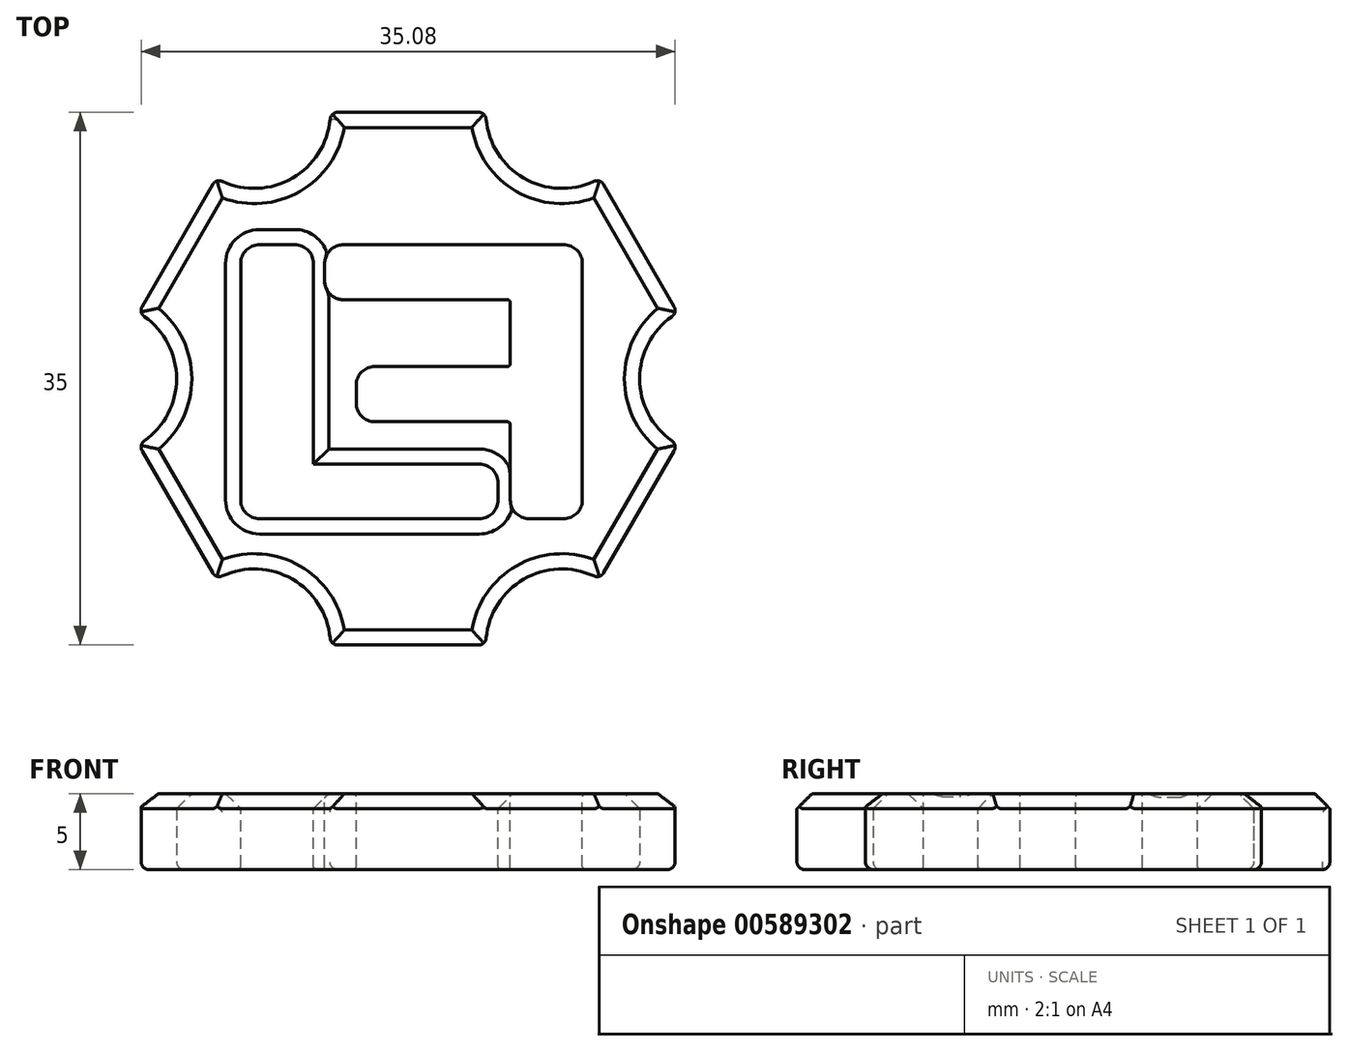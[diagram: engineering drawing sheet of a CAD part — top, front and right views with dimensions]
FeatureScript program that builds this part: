
annotation { "Feature Type Name" : "Feature", "Feature Type Description" : "" }
export const myFeature = defineFeature(function(context is Context, id is Id, definition is map)
    precondition{}
    {
        {
            var Q0;
            Q0=qCreatedBy(makeId("Top.planeOp"),FACE);
            var sketch = newSketch(context, id + "F0", { "sketchPlane" : qUnion([Q0])});
            skCircle(sketch, "E0.cCircle", {"center": v(0, 0) * mm, "radius": 17.5 * mm, "construction": true});
            skLineSegment(sketch, "E0.0", {"start": v(10.1, -17.5) * mm, "end": v(-10.1, -17.5) * mm});
            skLineSegment(sketch, "E0.1", {"start": v(-10.1, -17.5) * mm, "end": v(-20.2, 0) * mm});
            skLineSegment(sketch, "E0.2", {"start": v(-20.2, 0) * mm, "end": v(-10.1, 17.5) * mm});
            skLineSegment(sketch, "E0.3", {"start": v(-10.1, 17.5) * mm, "end": v(10.1, 17.5) * mm});
            skLineSegment(sketch, "E0.4", {"start": v(10.1, 17.5) * mm, "end": v(20.2, 0) * mm});
            skLineSegment(sketch, "E0.5", {"start": v(20.2, 0) * mm, "end": v(10.1, -17.5) * mm});
            skPoint(sketch, "E0.0.midPoint", {"position": v(0, -17.5) * mm});
            skCircle(sketch, "E1", {"center": v(-10.1, 17.5) * mm, "radius": 5 * mm});
            skCircle(sketch, "E2", {"center": v(-20.2, 0) * mm, "radius": 5 * mm});
            skCircle(sketch, "E3", {"center": v(-10.1, -17.5) * mm, "radius": 5 * mm});
            skCircle(sketch, "E4", {"center": v(10.1, -17.5) * mm, "radius": 5 * mm});
            skCircle(sketch, "E5", {"center": v(20.2, 0) * mm, "radius": 5 * mm});
            skCircle(sketch, "E6", {"center": v(10.1, 17.5) * mm, "radius": 5 * mm});
            skSolve(sketch);
        }
        {
            var Q0;
            {var subQ1=sQuery(id+"F0.wireOp",EDGE,"E0.0");var subQ13=sQuery(id+"F0.wireOp",EDGE,"E4");var subQ15=makeQuery(id+"F0.imprint","INTERSECT",VERTEX,{"derivedFrom":[subQ1,subQ13]});Q0=makeQuery(id+"F0.imprint","IMPRINT",FACE,{"disambiguationData":[TD([[makeQuery(id+"F0.imprint","IMPRINT",EDGE,{"disambiguationData":[TD([[subQ15,-1.0]])],"derivedFrom":subQ1}),-1.0]])]});}
            extrude(context, id + "F1", {"entities" : qUnion([Q0]), "endBound" : BoundingType.SYMMETRIC, "depth" : 5 * mm, "offsetDistance" : 25 * mm});
        }
        {
            var Q0;
            Q0=makeQuery(id+"F1.opExtrude","CAP_FACE",FACE,{"disambiguationData":[OSD([sQuery(id+"F0.wireOp",EDGE,"E0.0"),sQuery(id+"F0.wireOp",EDGE,"E0.1"),sQuery(id+"F0.wireOp",EDGE,"E0.2"),sQuery(id+"F0.wireOp",EDGE,"E0.3"),sQuery(id+"F0.wireOp",EDGE,"E0.4"),sQuery(id+"F0.wireOp",EDGE,"E0.5"),sQuery(id+"F0.wireOp",EDGE,"E1"),sQuery(id+"F0.wireOp",EDGE,"E2"),sQuery(id+"F0.wireOp",EDGE,"E3"),sQuery(id+"F0.wireOp",EDGE,"E4"),sQuery(id+"F0.wireOp",EDGE,"E5"),sQuery(id+"F0.wireOp",EDGE,"E6")])],"isStart":false});
            var sketch = newSketch(context, id + "F2", { "sketchPlane" : qUnion([Q0])});
            skLineSegment(sketch, "E7", {"start": v(4.67, -5.61) * mm, "end": v(-6.22, -5.61) * mm});
            skArc(sketch, "E8", {"start": v(5.9, -6.85) * mm, "mid": v(5.54, -5.98) * mm, "end": v(4.67, -5.61) * mm});
            skLineSegment(sketch, "E9", {"start": v(5.9, -7.96) * mm, "end": v(5.9, -6.85) * mm});
            skArc(sketch, "E10", {"start": v(4.67, -9.2) * mm, "mid": v(5.54, -8.84) * mm, "end": v(5.9, -7.96) * mm});
            skLineSegment(sketch, "E11", {"start": v(-9.76, -9.2) * mm, "end": v(4.67, -9.2) * mm});
            skArc(sketch, "E12", {"start": v(-11, -7.96) * mm, "mid": v(-10.63, -8.84) * mm, "end": v(-9.76, -9.2) * mm});
            skArc(sketch, "E13", {"start": v(-9.76, 8.8) * mm, "mid": v(-10.63, 8.44) * mm, "end": v(-11, 7.56) * mm});
            skLineSegment(sketch, "E14", {"start": v(-7.45, 8.8) * mm, "end": v(-9.76, 8.8) * mm});
            skLineSegment(sketch, "E15", {"start": v(-6.22, -5.61) * mm, "end": v(-6.22, 7.56) * mm});
            skArc(sketch, "E16", {"start": v(-6.22, 7.56) * mm, "mid": v(-6.58, 8.44) * mm, "end": v(-7.45, 8.8) * mm});
            skLineSegment(sketch, "E17", {"start": v(-11, 7.56) * mm, "end": v(-11, -7.96) * mm});
            skArc(sketch, "E18", {"start": v(10.2, -9.2) * mm, "mid": v(11.08, -8.84) * mm, "end": v(11.44, -7.96) * mm});
            skLineSegment(sketch, "E19", {"start": v(7.95, -9.2) * mm, "end": v(10.2, -9.2) * mm});
            skArc(sketch, "E20", {"start": v(6.71, -7.96) * mm, "mid": v(7.07, -8.84) * mm, "end": v(7.95, -9.2) * mm});
            skLineSegment(sketch, "E21", {"start": v(6.71, -2.83) * mm, "end": v(6.71, -7.96) * mm});
            skLineSegment(sketch, "E22", {"start": v(-2.18, -2.83) * mm, "end": v(6.71, -2.83) * mm});
            skArc(sketch, "E23", {"start": v(-3.41, -1.6) * mm, "mid": v(-3.05, -2.47) * mm, "end": v(-2.18, -2.83) * mm});
            skLineSegment(sketch, "E24", {"start": v(-3.41, -0.44) * mm, "end": v(-3.41, -1.6) * mm});
            skArc(sketch, "E25", {"start": v(-2.18, 0.8) * mm, "mid": v(-3.05, 0.44) * mm, "end": v(-3.41, -0.44) * mm});
            skLineSegment(sketch, "E26", {"start": v(6.71, 0.8) * mm, "end": v(-2.18, 0.8) * mm});
            skArc(sketch, "E27", {"start": v(-4.25, 8.8) * mm, "mid": v(-5.12, 8.44) * mm, "end": v(-5.48, 7.56) * mm});
            skArc(sketch, "E28", {"start": v(11.44, 7.56) * mm, "mid": v(11.08, 8.44) * mm, "end": v(10.2, 8.8) * mm});
            skArc(sketch, "E29", {"start": v(-5.48, 6.43) * mm, "mid": v(-5.12, 5.55) * mm, "end": v(-4.25, 5.2) * mm});
            skLineSegment(sketch, "E30", {"start": v(6.71, 5.2) * mm, "end": v(6.71, 0.8) * mm});
            skLineSegment(sketch, "E31", {"start": v(-4.25, 5.2) * mm, "end": v(6.71, 5.2) * mm});
            skLineSegment(sketch, "E32", {"start": v(-5.48, 7.56) * mm, "end": v(-5.48, 6.43) * mm});
            skLineSegment(sketch, "E33", {"start": v(10.2, 8.8) * mm, "end": v(-4.25, 8.8) * mm});
            skLineSegment(sketch, "E34", {"start": v(11.44, -7.96) * mm, "end": v(11.44, 7.56) * mm});
            skSolve(sketch);
        }
        {
            var Q0;
            Q0 = qSketchRegion(id + "F2", true);
            extrude(context, id + "F3", {"entities" : qUnion([Q0]), "operationType" : NewBodyOperationType.REMOVE, "oppositeDirection" : true, "depth" : 25 * mm, "offsetDistance" : 25 * mm});
        }
        {
            var Q0;
            Q0=makeQuery(id+"F3.boolean.opBoolean","COPY",EDGE,{"derivedFrom":makeQuery(id+"F3.opExtrude","CAP_EDGE",EDGE,{"disambiguationData":[OSD([sQuery(id+"F2.wireOp",EDGE,"E17")])],"isStart":true})});
            var Q1;
            Q1=makeQuery(id+"F3.boolean.opBoolean","INTERSECT",EDGE,{"derivedFrom":[makeQuery(id+"F1.opExtrude","CAP_FACE",FACE,{"disambiguationData":[OSD([sQuery(id+"F0.wireOp",EDGE,"E0.0"),sQuery(id+"F0.wireOp",EDGE,"E0.1"),sQuery(id+"F0.wireOp",EDGE,"E0.2"),sQuery(id+"F0.wireOp",EDGE,"E0.3"),sQuery(id+"F0.wireOp",EDGE,"E0.4"),sQuery(id+"F0.wireOp",EDGE,"E0.5"),sQuery(id+"F0.wireOp",EDGE,"E1"),sQuery(id+"F0.wireOp",EDGE,"E2"),sQuery(id+"F0.wireOp",EDGE,"E3"),sQuery(id+"F0.wireOp",EDGE,"E4"),sQuery(id+"F0.wireOp",EDGE,"E5"),sQuery(id+"F0.wireOp",EDGE,"E6")])],"isStart":true}),makeQuery(id+"F3.opExtrude","SWEPT_FACE",FACE,{"disambiguationData":[OSD([sQuery(id+"F2.wireOp",EDGE,"E17")])]})]});
            var Q2;
            Q2=makeQuery(id+"F3.boolean.opBoolean","INTERSECT",EDGE,{"derivedFrom":[makeQuery(id+"F1.opExtrude","CAP_FACE",FACE,{"disambiguationData":[OSD([sQuery(id+"F0.wireOp",EDGE,"E0.0"),sQuery(id+"F0.wireOp",EDGE,"E0.1"),sQuery(id+"F0.wireOp",EDGE,"E0.2"),sQuery(id+"F0.wireOp",EDGE,"E0.3"),sQuery(id+"F0.wireOp",EDGE,"E0.4"),sQuery(id+"F0.wireOp",EDGE,"E0.5"),sQuery(id+"F0.wireOp",EDGE,"E1"),sQuery(id+"F0.wireOp",EDGE,"E2"),sQuery(id+"F0.wireOp",EDGE,"E3"),sQuery(id+"F0.wireOp",EDGE,"E4"),sQuery(id+"F0.wireOp",EDGE,"E5"),sQuery(id+"F0.wireOp",EDGE,"E6")])],"isStart":true}),makeQuery(id+"F3.opExtrude","SWEPT_FACE",FACE,{"disambiguationData":[OSD([sQuery(id+"F2.wireOp",EDGE,"E34")])]})]});
            var Q3;
            Q3=makeQuery(id+"F3.boolean.opBoolean","COPY",EDGE,{"derivedFrom":makeQuery(id+"F3.opExtrude","CAP_EDGE",EDGE,{"disambiguationData":[OSD([sQuery(id+"F2.wireOp",EDGE,"E34")])],"isStart":true})});
            var Q4;
            Q4=makeQuery(id+"F3.boolean.opBoolean","COPY",FACE,{"derivedFrom":makeQuery(id+"F3.opExtrude","SWEPT_FACE",FACE,{"disambiguationData":[OSD([sQuery(id+"F2.wireOp",EDGE,"E30")])]})});
            var Q5;
            Q5=makeQuery(id+"F3.boolean.opBoolean","COPY",FACE,{"derivedFrom":makeQuery(id+"F3.opExtrude","SWEPT_FACE",FACE,{"disambiguationData":[OSD([sQuery(id+"F2.wireOp",EDGE,"E21")])]})});
            var Q6;
            Q6=makeQuery(id+"F3.boolean.opBoolean","COPY",FACE,{"derivedFrom":makeQuery(id+"F3.opExtrude","SWEPT_FACE",FACE,{"disambiguationData":[OSD([sQuery(id+"F2.wireOp",EDGE,"E22")])]})});
            fillet(context, id + "F4", {"entities" : qUnion([Q0, Q1, Q2, Q3, Q4, Q5, Q6]), "radius" : .2 * mm, "tangentPropagation" : true, "allowEdgeOverflow" : false});
        }
        {
            var Q0;
            Q0=makeQuery(id+"F1.opExtrude","CAP_FACE",FACE,{"disambiguationData":[OSD([sQuery(id+"F0.wireOp",EDGE,"E0.0"),sQuery(id+"F0.wireOp",EDGE,"E0.1"),sQuery(id+"F0.wireOp",EDGE,"E0.2"),sQuery(id+"F0.wireOp",EDGE,"E0.3"),sQuery(id+"F0.wireOp",EDGE,"E0.4"),sQuery(id+"F0.wireOp",EDGE,"E0.5"),sQuery(id+"F0.wireOp",EDGE,"E1"),sQuery(id+"F0.wireOp",EDGE,"E2"),sQuery(id+"F0.wireOp",EDGE,"E3"),sQuery(id+"F0.wireOp",EDGE,"E4"),sQuery(id+"F0.wireOp",EDGE,"E5"),sQuery(id+"F0.wireOp",EDGE,"E6")])],"isStart":false});
            chamfer(context, id + "F5", {"entities" : qUnion([Q0]), "width" : 1 * mm, "tangentPropagation" : true});
        }
        {
            var Q0;
            Q0=makeQuery(id+"F1.opExtrude","CAP_FACE",FACE,{"disambiguationData":[OSD([sQuery(id+"F0.wireOp",EDGE,"E0.0"),sQuery(id+"F0.wireOp",EDGE,"E0.1"),sQuery(id+"F0.wireOp",EDGE,"E0.2"),sQuery(id+"F0.wireOp",EDGE,"E0.3"),sQuery(id+"F0.wireOp",EDGE,"E0.4"),sQuery(id+"F0.wireOp",EDGE,"E0.5"),sQuery(id+"F0.wireOp",EDGE,"E1"),sQuery(id+"F0.wireOp",EDGE,"E2"),sQuery(id+"F0.wireOp",EDGE,"E3"),sQuery(id+"F0.wireOp",EDGE,"E4"),sQuery(id+"F0.wireOp",EDGE,"E5"),sQuery(id+"F0.wireOp",EDGE,"E6")])],"isStart":true});
            var Q1;
            Q1=makeQuery(id+"F1.opExtrude","SWEPT_EDGE",EDGE,{"disambiguationData":[OSD([sQuery(id+"F0.wireOp",EDGE,"E0.3"),sQuery(id+"F0.wireOp",EDGE,"E6")])]});
            var Q2;
            Q2=makeQuery(id+"F1.opExtrude","SWEPT_EDGE",EDGE,{"disambiguationData":[OSD([sQuery(id+"F0.wireOp",EDGE,"E0.3"),sQuery(id+"F0.wireOp",EDGE,"E1")])]});
            var Q3;
            Q3=makeQuery(id+"F1.opExtrude","SWEPT_FACE",FACE,{"disambiguationData":[OSD([sQuery(id+"F0.wireOp",EDGE,"E1")])]});
            var Q4;
            Q4=makeQuery(id+"F1.opExtrude","SWEPT_EDGE",EDGE,{"disambiguationData":[OSD([sQuery(id+"F0.wireOp",EDGE,"E0.2"),sQuery(id+"F0.wireOp",EDGE,"E2")])]});
            var Q5;
            Q5=makeQuery(id+"F1.opExtrude","SWEPT_EDGE",EDGE,{"disambiguationData":[OSD([sQuery(id+"F0.wireOp",EDGE,"E0.1"),sQuery(id+"F0.wireOp",EDGE,"E2")])]});
            var Q6;
            Q6=makeQuery(id+"F1.opExtrude","SWEPT_EDGE",EDGE,{"disambiguationData":[OSD([sQuery(id+"F0.wireOp",EDGE,"E0.1"),sQuery(id+"F0.wireOp",EDGE,"E3")])]});
            var Q7;
            Q7=makeQuery(id+"F1.opExtrude","SWEPT_EDGE",EDGE,{"disambiguationData":[OSD([sQuery(id+"F0.wireOp",EDGE,"E0.0"),sQuery(id+"F0.wireOp",EDGE,"E3")])]});
            var Q8;
            Q8=makeQuery(id+"F1.opExtrude","SWEPT_EDGE",EDGE,{"disambiguationData":[OSD([sQuery(id+"F0.wireOp",EDGE,"E0.0"),sQuery(id+"F0.wireOp",EDGE,"E4")])]});
            var Q9;
            Q9=makeQuery(id+"F1.opExtrude","SWEPT_EDGE",EDGE,{"disambiguationData":[OSD([sQuery(id+"F0.wireOp",EDGE,"E0.5"),sQuery(id+"F0.wireOp",EDGE,"E4")])]});
            var Q10;
            Q10=makeQuery(id+"F1.opExtrude","SWEPT_EDGE",EDGE,{"disambiguationData":[OSD([sQuery(id+"F0.wireOp",EDGE,"E0.5"),sQuery(id+"F0.wireOp",EDGE,"E5")])]});
            var Q11;
            Q11=makeQuery(id+"F1.opExtrude","SWEPT_EDGE",EDGE,{"disambiguationData":[OSD([sQuery(id+"F0.wireOp",EDGE,"E0.4"),sQuery(id+"F0.wireOp",EDGE,"E5")])]});
            var Q12;
            Q12=makeQuery(id+"F1.opExtrude","SWEPT_EDGE",EDGE,{"disambiguationData":[OSD([sQuery(id+"F0.wireOp",EDGE,"E0.4"),sQuery(id+"F0.wireOp",EDGE,"E6")])]});
            fillet(context, id + "F6", {"entities" : qUnion([Q0, Q1, Q2, Q3, Q4, Q5, Q6, Q7, Q8, Q9, Q10, Q11, Q12]), "radius" : .5 * mm, "tangentPropagation" : true, "allowEdgeOverflow" : false});
        }
    });
